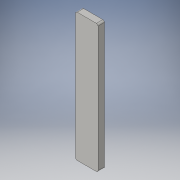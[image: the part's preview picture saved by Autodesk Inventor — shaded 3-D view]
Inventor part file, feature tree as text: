
AUTODESK INVENTOR PART (.ipt)
format: ipt  version: 2016 (Build 200138000, 138)  size: 105,984 bytes
history: native  units: in
note: dims shown in document units (in); Inventor stores cm internally (conversion verified against a paired STEP export)
features: reference x4, extrude x1, fillet x1, sketch x1
ambient origin geometry x8: Origin, YZ Plane, XZ Plane, XY Plane, X Axis, Y Axis, Z Axis, Center Point
bodies: Body1 (feature_tree)
feature tree (7):
  extrude  "Extrusion2"  Depth=0.0394in
  fillet  "Fillet1"  Radius=0.0787in
  sketch  "Sketch1"  dims[d0=0.0787in d1=0.0787in d2=0.0787in d3=0.0787in d8=3.142in d9=2.591in d11=0.1575in d12=0.0in d13=0.0394in]
  reference  "Reference1"
  reference  "Reference2"
  reference  "Reference3"
  reference  "Reference4"
